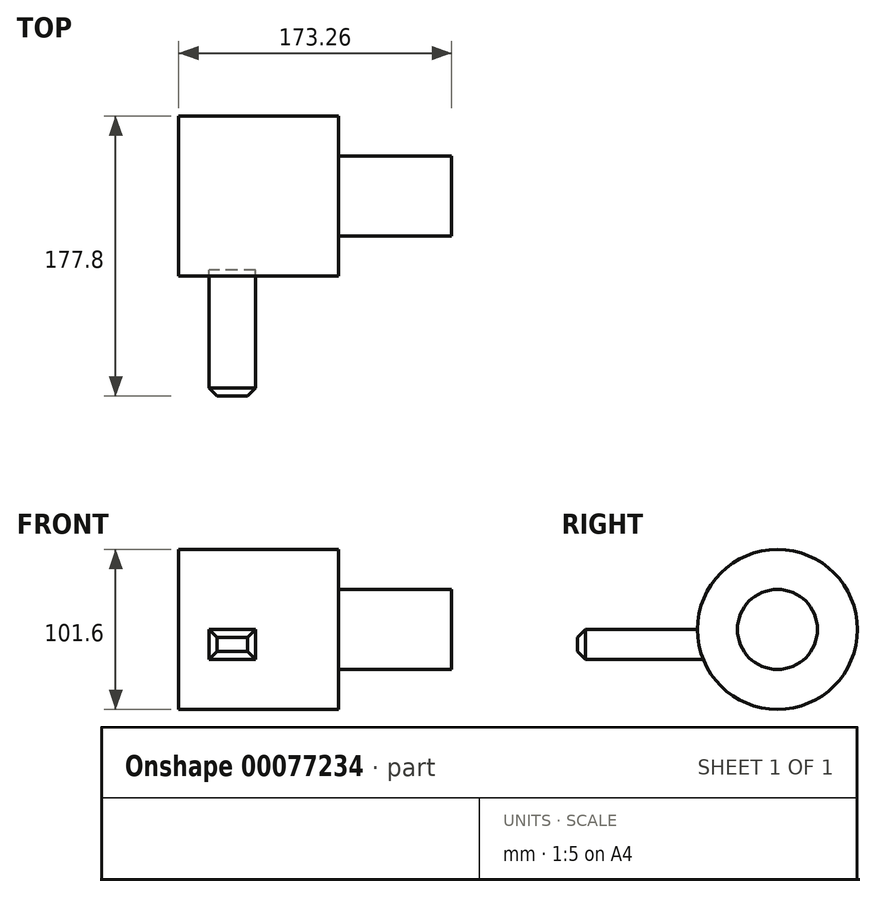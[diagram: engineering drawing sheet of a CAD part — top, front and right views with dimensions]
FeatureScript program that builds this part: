
annotation { "Feature Type Name" : "Feature", "Feature Type Description" : "" }
export const myFeature = defineFeature(function(context is Context, id is Id, definition is map)
    precondition{}
    {
        {
            var Q0;
            Q0=qCreatedBy(makeId("Front.planeOp"),FACE);
            var sketch = newSketch(context, id + "F0", { "sketchPlane" : qUnion([Q0])});
            skLineSegment(sketch, "E0.bottom", {"start": v(-46.26, 50.8) * mm, "end": v(55.34, 50.8) * mm});
            skLineSegment(sketch, "E0.top", {"start": v(-46.26, 0) * mm, "end": v(55.34, 0) * mm});
            skLineSegment(sketch, "E0.left", {"start": v(-46.26, 50.8) * mm, "end": v(-46.26, 0) * mm});
            skLineSegment(sketch, "E0.right", {"start": v(55.34, 50.8) * mm, "end": v(55.34, 0) * mm});
            skLineSegment(sketch, "E1", {"start": v(12.57, 0) * mm, "end": v(-100.69, 0) * mm});
            skPoint(sketch, "E1.endSnap0", {"position": v(4.54, 0) * mm});
            skSolve(sketch);
        }
        {
            var Q0;
            Q0 = qSketchRegion(id + "F0", true);
            var Q1;
            Q1=sQuery(id+"F0.wireOp",EDGE,"E0.top");
            revolve(context, id + "F1", {"entities" : qUnion([Q0]), "axis" : qUnion([Q1]), "revolveType" : RevolveType.FULL});
        }
        {
            var Q0;
            Q0=qCreatedBy(makeId("Right.planeOp"),FACE);
            var sketch = newSketch(context, id + "F2", { "sketchPlane" : qUnion([Q0])});
            skCircle(sketch, "E2", {"center": v(0, 0) * mm, "radius": 25.4 * mm});
            skSolve(sketch);
        }
        {
            var Q0;
            Q0 = qSketchRegion(id + "F2", true);
            extrude(context, id + "F3", {"entities" : qUnion([Q0]), "operationType" : NewBodyOperationType.ADD, "depth" : 127 * mm});
        }
        {
            var Q0;
            Q0=qCreatedBy(makeId("Front.planeOp"),FACE);
            var sketch = newSketch(context, id + "F4", { "sketchPlane" : qUnion([Q0])});
            skLineSegment(sketch, "E3.bottom", {"start": v(2.59, 0) * mm, "end": v(-27, 0) * mm});
            skLineSegment(sketch, "E3.top", {"start": v(2.59, -18.93) * mm, "end": v(-27, -18.93) * mm});
            skLineSegment(sketch, "E3.left", {"start": v(2.59, 0) * mm, "end": v(2.59, -18.93) * mm});
            skLineSegment(sketch, "E3.right", {"start": v(-27, 0) * mm, "end": v(-27, -18.93) * mm});
            skPoint(sketch, "E4.oppositeSnap0", {"position": v(2.59, -9.46) * mm});
            skSolve(sketch);
        }
        {
            var Q0;
            Q0 = qSketchRegion(id + "F4", true);
            extrude(context, id + "F5", {"entities" : qUnion([Q0]), "operationType" : NewBodyOperationType.ADD, "depth" : 127 * mm});
        }
        {
            var Q0;
            Q0=makeQuery(id+"F5.opExtrude","CAP_FACE",FACE,{"disambiguationData":[OSD([sQuery(id+"F4.wireOp",EDGE,"E3.bottom"),sQuery(id+"F4.wireOp",EDGE,"E3.top"),sQuery(id+"F4.wireOp",EDGE,"E3.left"),sQuery(id+"F4.wireOp",EDGE,"E3.right")])],"isStart":false});
            chamfer(context, id + "F6", {"entities" : qUnion([Q0]), "chamferType" : ChamferType.OFFSET_ANGLE, "width" : 5.08 * mm, "oppositeDirection" : false, "angle" : 45 * degree, "tangentPropagation" : true});
        }
    });
